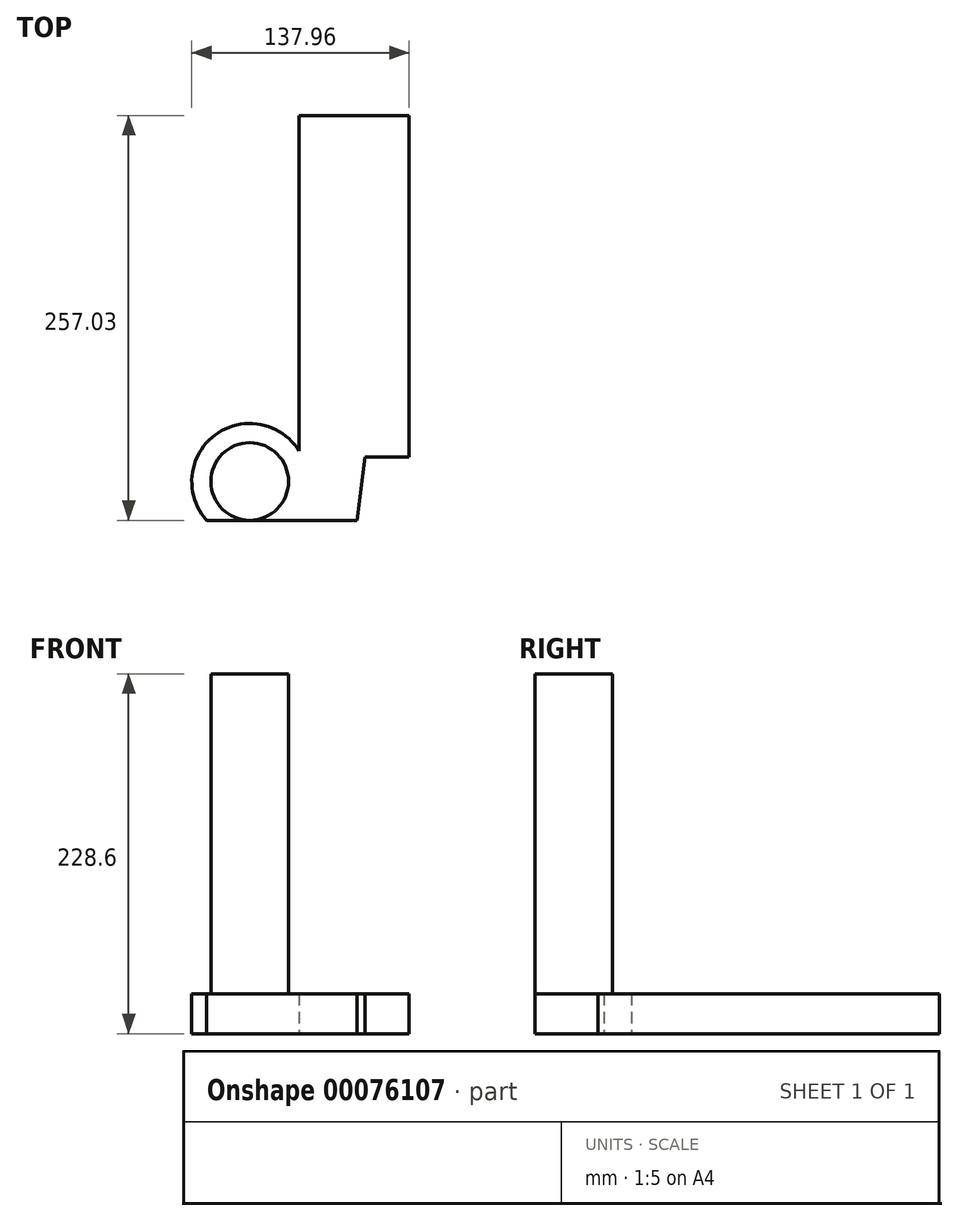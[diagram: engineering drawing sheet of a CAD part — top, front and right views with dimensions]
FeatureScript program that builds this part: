
annotation { "Feature Type Name" : "Feature", "Feature Type Description" : "" }
export const myFeature = defineFeature(function(context is Context, id is Id, definition is map)
    precondition{}
    {
        {
            var Q0;
            Q0=qCreatedBy(makeId("Top.planeOp"),FACE);
            var sketch = newSketch(context, id + "F0", { "sketchPlane" : qUnion([Q0])});
            skLineSegment(sketch, "E0", {"start": v(-250.32, -98.86) * mm, "end": v(-250.32, 114.3) * mm});
            skLineSegment(sketch, "E1", {"start": v(-250.32, 114.3) * mm, "end": v(-180.52, 114.3) * mm});
            skLineSegment(sketch, "E2", {"start": v(-180.52, 114.3) * mm, "end": v(-180.52, -102.6) * mm});
            skLineSegment(sketch, "E3", {"start": v(-180.52, -102.6) * mm, "end": v(-208.4, -102.6) * mm});
            skLineSegment(sketch, "E4", {"start": v(-208.4, -102.6) * mm, "end": v(-213.43, -142.73) * mm});
            skLineSegment(sketch, "E5", {"start": v(-213.43, -142.73) * mm, "end": v(-309, -142.73) * mm});
            skArc(sketch, "E6", {"start": v(-250.32, -98.86) * mm, "mid": v(-303.72, -88.61) * mm, "end": v(-309, -142.73) * mm});
            skSolve(sketch);
        }
        {
            var Q0;
            Q0=makeQuery(id+"F0.imprint","IMPRINT",FACE,{"disambiguationData":[TD([[makeQuery(id+"F0.imprint","IMPRINT",EDGE,{"derivedFrom":sQuery(id+"F0.wireOp",EDGE,"E0")}),-1.0]])]});
            extrude(context, id + "F1", {"entities" : qUnion([Q0]), "depth" : 25.4 * mm});
        }
        {
            var Q0;
            Q0=makeQuery(id+"F1.opExtrude","CAP_FACE",FACE,{"disambiguationData":[OSD([sQuery(id+"F0.wireOp",EDGE,"E0"),sQuery(id+"F0.wireOp",EDGE,"E1"),sQuery(id+"F0.wireOp",EDGE,"E2"),sQuery(id+"F0.wireOp",EDGE,"E3"),sQuery(id+"F0.wireOp",EDGE,"E4"),sQuery(id+"F0.wireOp",EDGE,"E5"),sQuery(id+"F0.wireOp",EDGE,"E6")])],"isStart":false});
            var sketch = newSketch(context, id + "F2", { "sketchPlane" : qUnion([Q0])});
            skCircle(sketch, "E7", {"center": v(-281.69, -118.08) * mm, "radius": 24.64 * mm});
            skSolve(sketch);
        }
        {
            var Q0;
            Q0=makeQuery(id+"F2.imprint","IMPRINT",FACE,{"disambiguationData":[TD([[makeQuery(id+"F2.imprint","IMPRINT",EDGE,{"derivedFrom":sQuery(id+"F2.wireOp",EDGE,"E7")}),1.0]])]});
            extrude(context, id + "F3", {"entities" : qUnion([Q0]), "operationType" : NewBodyOperationType.ADD, "depth" : 203.2 * mm});
        }
    });
